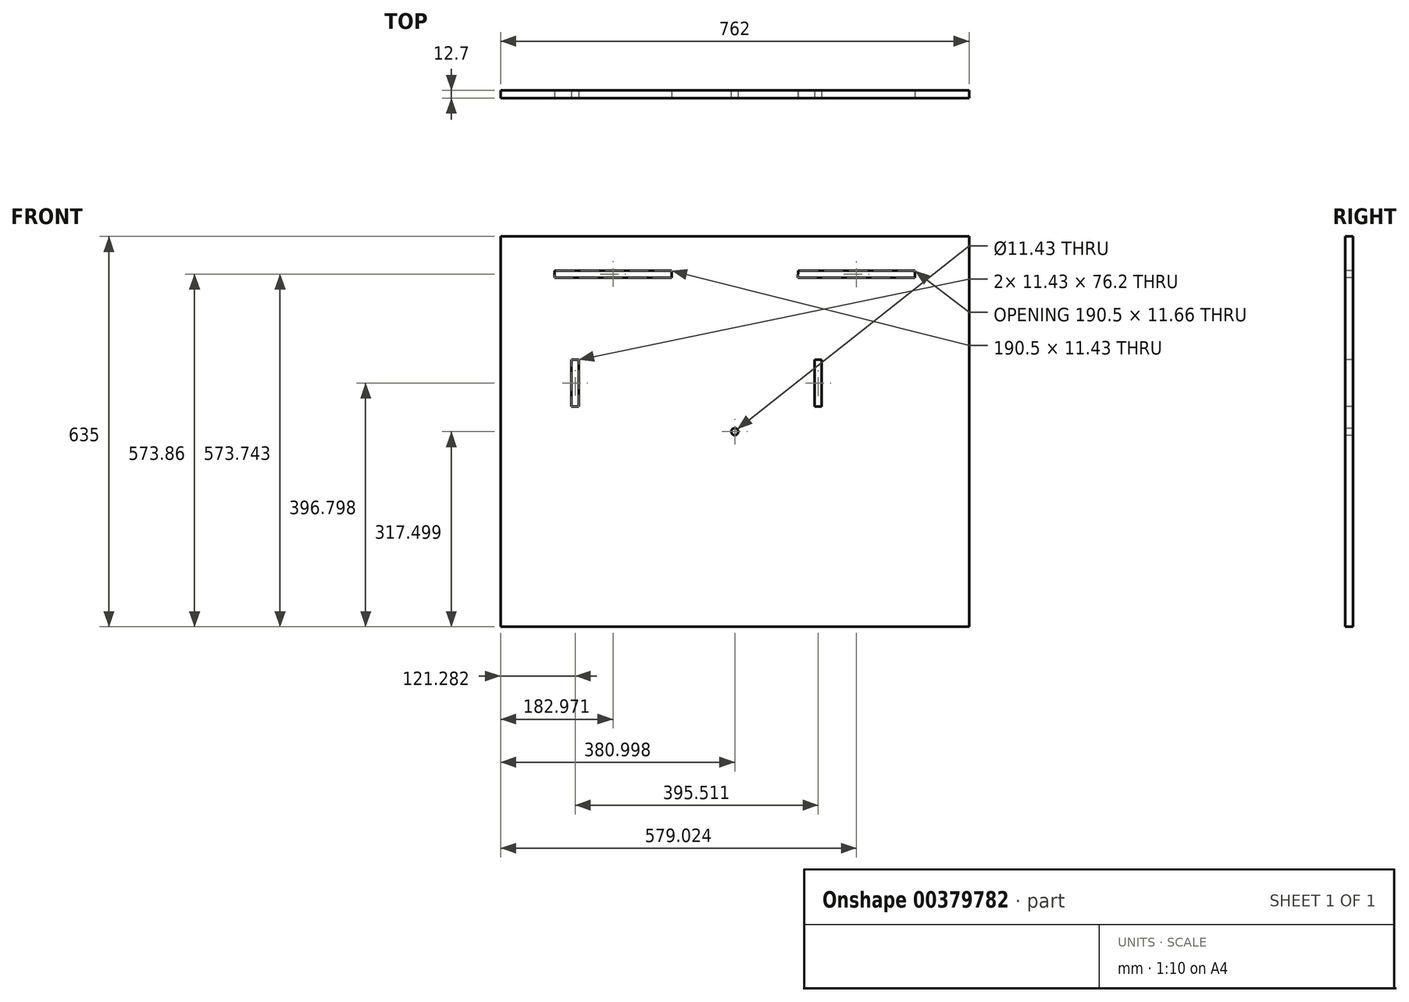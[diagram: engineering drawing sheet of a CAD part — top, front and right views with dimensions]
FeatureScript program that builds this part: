
annotation { "Feature Type Name" : "Feature", "Feature Type Description" : "" }
export const myFeature = defineFeature(function(context is Context, id is Id, definition is map)
    precondition{}
    {
        {
            var Q0;
            Q0=qCreatedBy(makeId("Front.planeOp"),FACE);
            var sketch = newSketch(context, id + "F0", { "sketchPlane" : qUnion([Q0])});
            skLineSegment(sketch, "E0.bottom", {"start": v(-75.3, 558.6) * mm, "end": v(686.7, 558.6) * mm});
            skLineSegment(sketch, "E0.top", {"start": v(-75.3, -76.4) * mm, "end": v(686.7, -76.4) * mm});
            skLineSegment(sketch, "E0.left", {"start": v(-75.3, 558.6) * mm, "end": v(-75.3, -76.4) * mm});
            skLineSegment(sketch, "E0.right", {"start": v(686.7, 558.6) * mm, "end": v(686.7, -76.4) * mm});
            skLineSegment(sketch, "E1", {"start": v(305.7, 558.6) * mm, "end": v(305.7, -76.4) * mm, "construction": true});
            skLineSegment(sketch, "E2", {"start": v(-75.3, 241.1) * mm, "end": v(686.7, 241.1) * mm, "construction": true});
            skCircle(sketch, "E3", {"center": v(305.7, 241.1) * mm, "radius": 5.72 * mm});
            skSolve(sketch);
        }
        {
            var Q0;
            Q0 = qSketchRegion(id + "F0", true);
            extrude(context, id + "F1", {"entities" : qUnion([Q0]), "depth" : 12.7 * mm});
        }
        {
            var Q0;
            Q0=makeQuery(id+"F1.opExtrude","CAP_FACE",FACE,{"disambiguationData":[OSD([sQuery(id+"F0.wireOp",EDGE,"E0.bottom"),sQuery(id+"F0.wireOp",EDGE,"E0.top"),sQuery(id+"F0.wireOp",EDGE,"E0.left"),sQuery(id+"F0.wireOp",EDGE,"E0.right"),sQuery(id+"F0.wireOp",EDGE,"E3")])],"isStart":false});
            var sketch = newSketch(context, id + "F2", { "sketchPlane" : qUnion([Q0])});
            skLineSegment(sketch, "E4.MirrorCS", {"start": v(51.7, 358.5) * mm, "end": v(51.7, 282.3) * mm});
            skLineSegment(sketch, "E5.MirrorCS", {"start": v(40.28, 358.5) * mm, "end": v(40.28, 282.3) * mm});
            skLineSegment(sketch, "E6.MirrorCS", {"start": v(51.7, 282.3) * mm, "end": v(40.28, 282.3) * mm});
            skLineSegment(sketch, "E7.MirrorCS", {"start": v(51.7, 358.5) * mm, "end": v(40.28, 358.5) * mm});
            skLineSegment(sketch, "E8", {"start": v(45.45, 491.75) * mm, "end": v(12.43, 491.75) * mm});
            skLineSegment(sketch, "E9", {"start": v(45.45, 491.75) * mm, "end": v(202.93, 491.75) * mm});
            skLineSegment(sketch, "E10", {"start": v(12.43, 491.75) * mm, "end": v(12.43, 503.18) * mm});
            skLineSegment(sketch, "E11", {"start": v(12.43, 503.18) * mm, "end": v(202.85, 503.18) * mm});
            skLineSegment(sketch, "E12", {"start": v(202.85, 503.18) * mm, "end": v(202.93, 491.75) * mm});
            skLineSegment(sketch, "E13", {"start": v(46, 358.5) * mm, "end": v(45.45, 491.75) * mm});
            skLineSegment(sketch, "E14", {"start": v(305.7, 241.1) * mm, "end": v(305.7, 558.6) * mm});
            skLineSegment(sketch, "E15.MirrorCS", {"start": v(598.98, 503.18) * mm, "end": v(408.57, 503.18) * mm});
            skLineSegment(sketch, "E16.MirrorCS", {"start": v(598.98, 491.75) * mm, "end": v(598.98, 503.18) * mm});
            skLineSegment(sketch, "E17.MirrorCS", {"start": v(408.57, 503.18) * mm, "end": v(408.48, 491.75) * mm});
            skLineSegment(sketch, "E18", {"start": v(408.48, 491.75) * mm, "end": v(441.5, 491.51) * mm});
            skLineSegment(sketch, "E19", {"start": v(441.5, 491.51) * mm, "end": v(441.5, 358.26) * mm});
            skLineSegment(sketch, "E20", {"start": v(441.5, 358.26) * mm, "end": v(435.79, 358.26) * mm});
            skLineSegment(sketch, "E21", {"start": v(441.5, 358.26) * mm, "end": v(447.22, 358.26) * mm});
            skLineSegment(sketch, "E22", {"start": v(447.22, 358.26) * mm, "end": v(447.22, 282.06) * mm});
            skLineSegment(sketch, "E23", {"start": v(447.22, 282.06) * mm, "end": v(435.79, 282.06) * mm});
            skLineSegment(sketch, "E24", {"start": v(435.79, 358.26) * mm, "end": v(435.79, 282.06) * mm});
            skLineSegment(sketch, "E25", {"start": v(441.5, 491.51) * mm, "end": v(598.98, 491.75) * mm});
            skSolve(sketch);
        }
        {
            var Q0;
            Q0 = qSketchRegion(id + "F2", true);
            extrude(context, id + "F3", {"entities" : qUnion([Q0]), "operationType" : NewBodyOperationType.REMOVE, "oppositeDirection" : true, "depth" : 25.4 * mm});
        }
    });
